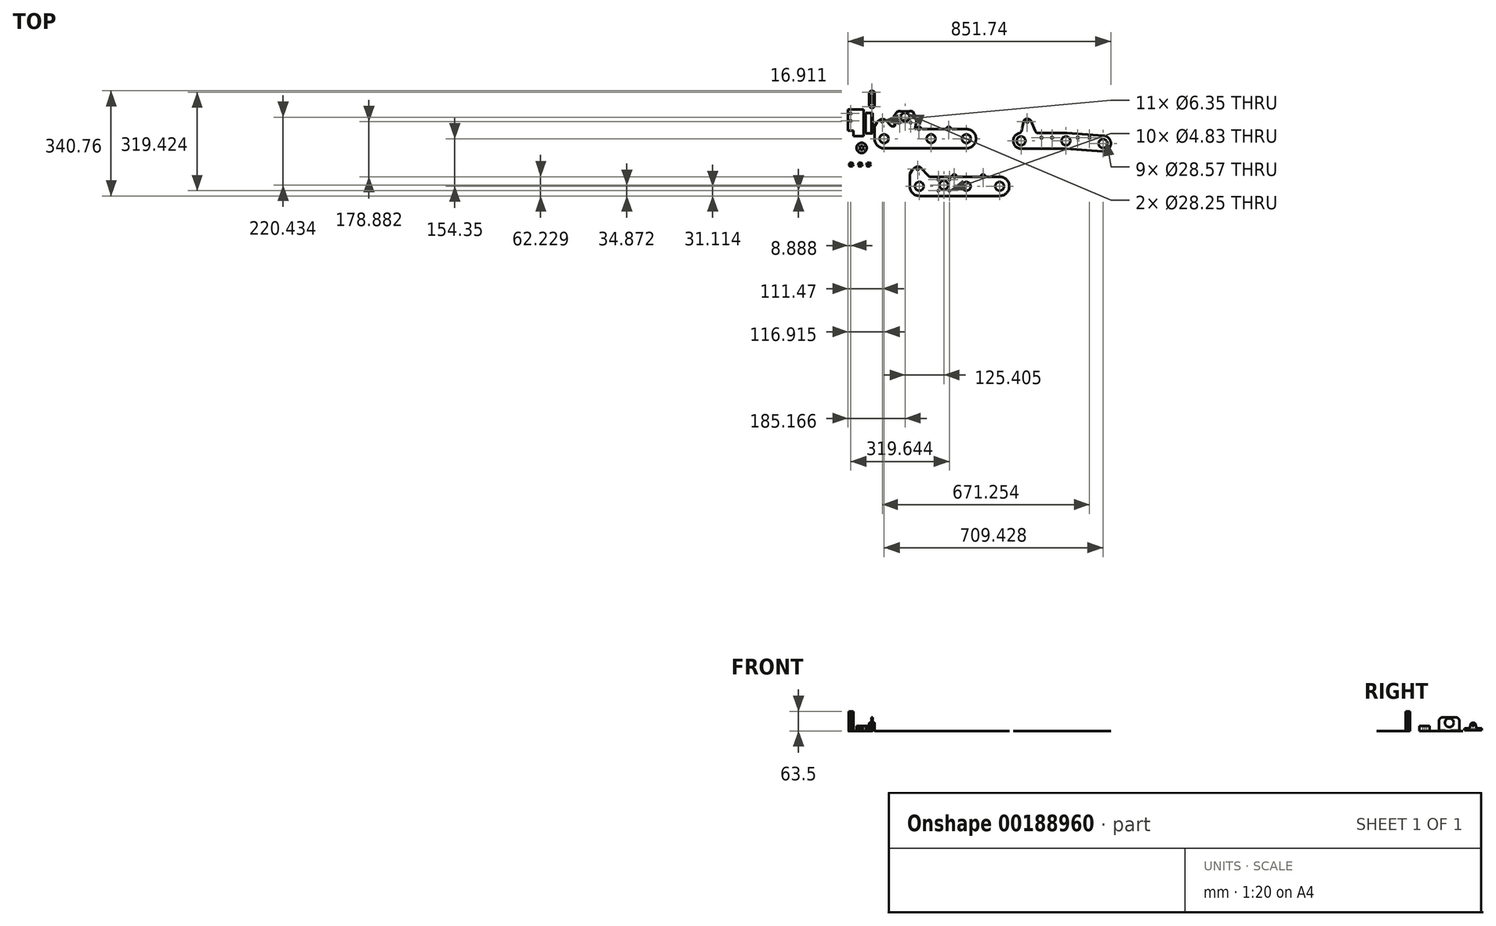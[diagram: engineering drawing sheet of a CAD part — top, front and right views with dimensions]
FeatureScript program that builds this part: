
annotation { "Feature Type Name" : "Feature", "Feature Type Description" : "" }
export const myFeature = defineFeature(function(context is Context, id is Id, definition is map)
    precondition{}
    {
        {
            assignVariable(context, id + "F0", {"name" : "width", "anyValue" : 16});
        }
        {
            var Q0;
            Q0=qCreatedBy(makeId("Top.planeOp"),FACE);
            var sketch = newSketch(context, id + "F1", { "sketchPlane" : qUnion([Q0])});
            skLineSegment(sketch, "E0", {"start": v(-68.88, 77.6) * mm, "end": v(-68.88, 9.01) * mm});
            skLineSegment(sketch, "E1", {"start": v(-68.88, 9.01) * mm, "end": v(-51.1, 9.01) * mm});
            skLineSegment(sketch, "E2", {"start": v(-51.1, 9.01) * mm, "end": v(-51.1, -8.77) * mm});
            skLineSegment(sketch, "E3", {"start": v(-51.1, -8.77) * mm, "end": v(-18.08, -8.77) * mm});
            skLineSegment(sketch, "E4", {"start": v(-18.08, -8.77) * mm, "end": v(-18.08, 9.01) * mm});
            skLineSegment(sketch, "E5", {"start": v(-18.08, 9.01) * mm, "end": v(-18.08, 77.6) * mm});
            skLineSegment(sketch, "E6", {"start": v(-18.08, 77.6) * mm, "end": v(-68.88, 77.6) * mm});
            skPoint(sketch, "E7", {"position": v(-60, 9.01) * mm});
            skCircle(sketch, "E8", {"center": v(-60, 40.12) * mm, "radius": 2.41 * mm});
            skCircle(sketch, "E9", {"center": v(-60, 64.05) * mm, "radius": 2.41 * mm});
            skLineSegment(sketch, "E10", {"start": v(-60, 40.12) * mm, "end": v(-60, 64.05) * mm, "construction": true});
            skSolve(sketch);
        }
        {
            var Q0;
            Q0=makeQuery(id+"F1.imprint","IMPRINT",FACE,{"disambiguationData":[TD([[makeQuery(id+"F1.imprint","IMPRINT",EDGE,{"derivedFrom":sQuery(id+"F1.wireOp",EDGE,"E0")}),1.0]])]});
            extrude(context, id + "F2", {"entities" : qUnion([Q0]), "depth" : 1 / 203.2 * mm});
        }
        {
            var Q0;
            Q0=qCreatedBy(makeId("Front.planeOp"),FACE);
            var sketch = newSketch(context, id + "F3", { "sketchPlane" : qUnion([Q0])});
            skLineSegment(sketch, "E11", {"start": v(-11.91, 0) * mm, "end": v(10.31, 0) * mm});
            skLineSegment(sketch, "E12", {"start": v(10.31, 0) * mm, "end": v(10.31, 44.45) * mm});
            skLineSegment(sketch, "E13", {"start": v(10.31, 44.45) * mm, "end": v(7.14, 44.45) * mm});
            skLineSegment(sketch, "E14", {"start": v(7.14, 44.45) * mm, "end": v(7.14, 3.18) * mm});
            skLineSegment(sketch, "E15", {"start": v(7.14, 3.18) * mm, "end": v(-11.91, 3.18) * mm});
            skLineSegment(sketch, "E16", {"start": v(-11.91, 3.17) * mm, "end": v(-11.91, 0) * mm});
            skSolve(sketch);
        }
        {
            var Q0;
            Q0 = qSketchRegion(id + "F3", true);
            extrude(context, id + "F4", {"entities" : qUnion([Q0]), "oppositeDirection" : true, "depth" : 66.04 * mm});
        }
        {
            var Q0;
            Q0=makeQuery(id+"F4.opExtrude","CAP_EDGE",EDGE,{"disambiguationData":[OSD([sQuery(id+"F3.wireOp",EDGE,"E13")])],"isStart":true});
            var Q1;
            Q1=makeQuery(id+"F4.opExtrude","CAP_EDGE",EDGE,{"disambiguationData":[OSD([sQuery(id+"F3.wireOp",EDGE,"E13")])],"isStart":false});
            chamfer(context, id + "F5", {"entities" : qUnion([Q0, Q1]), "width" : 7.62 * mm, "tangentPropagation" : true});
        }
        {
            var Q0;
            Q0=makeQuery(id+"F4.opExtrude","SWEPT_FACE",FACE,{"disambiguationData":[OSD([sQuery(id+"F3.wireOp",EDGE,"E12")])]});
            var sketch = newSketch(context, id + "F6", { "sketchPlane" : qUnion([Q0])});
            skCircle(sketch, "E17", {"center": v(33.02, 26.35) * mm, "radius": 14.29 * mm});
            skPoint(sketch, "E17.centerSnap0", {"position": v(33.02, 44.45) * mm});
            skSolve(sketch);
        }
        {
            var Q0;
            Q0 = qSketchRegion(id + "F6", true);
            extrude(context, id + "F7", {"entities" : qUnion([Q0]), "operationType" : NewBodyOperationType.REMOVE, "endBound" : BoundingType.THROUGH_ALL, "oppositeDirection" : true, "depth" : 25.4 * mm});
        }
        {
            var Q0;
            Q0=qCreatedBy(makeId("Top.planeOp"),FACE);
            var sketch = newSketch(context, id + "F8", { "sketchPlane" : qUnion([Q0])});
            skCircle(sketch, "E18", {"center": v(-29.26, -101.4) * mm, "radius": 2.55 * mm});
            skCircle(sketch, "E19.cCircle", {"center": v(-29.26, -101.4) * mm, "radius": 6.42 * mm, "construction": true});
            skLineSegment(sketch, "E19.0", {"start": v(-21.93, -100.32) * mm, "end": v(-24.66, -107.21) * mm});
            skLineSegment(sketch, "E19.1", {"start": v(-24.66, -107.21) * mm, "end": v(-32, -108.3) * mm});
            skLineSegment(sketch, "E19.2", {"start": v(-32, -108.3) * mm, "end": v(-36.6, -102.48) * mm});
            skLineSegment(sketch, "E19.3", {"start": v(-36.6, -102.48) * mm, "end": v(-33.86, -95.6) * mm});
            skLineSegment(sketch, "E19.4", {"start": v(-33.86, -95.6) * mm, "end": v(-26.53, -94.51) * mm});
            skLineSegment(sketch, "E19.5", {"start": v(-26.53, -94.51) * mm, "end": v(-21.93, -100.32) * mm});
            skPoint(sketch, "E19.0.midPoint", {"position": v(-23.3, -103.77) * mm});
            skCircle(sketch, "E20", {"center": v(-58.64, -101.4) * mm, "radius": 2.55 * mm});
            skCircle(sketch, "E21.cCircle", {"center": v(-58.64, -101.4) * mm, "radius": 6.42 * mm, "construction": true});
            skLineSegment(sketch, "E21.0", {"start": v(-51.3, -100.32) * mm, "end": v(-54.04, -107.21) * mm});
            skLineSegment(sketch, "E21.1", {"start": v(-54.04, -107.21) * mm, "end": v(-61.37, -108.3) * mm});
            skLineSegment(sketch, "E21.2", {"start": v(-61.37, -108.3) * mm, "end": v(-65.97, -102.48) * mm});
            skLineSegment(sketch, "E21.3", {"start": v(-65.97, -102.48) * mm, "end": v(-63.24, -95.6) * mm});
            skLineSegment(sketch, "E21.4", {"start": v(-63.24, -95.6) * mm, "end": v(-55.9, -94.51) * mm});
            skLineSegment(sketch, "E21.5", {"start": v(-55.9, -94.51) * mm, "end": v(-51.3, -100.32) * mm});
            skPoint(sketch, "E21.0.midPoint", {"position": v(-52.67, -103.77) * mm});
            skCircle(sketch, "E22", {"center": v(-2.45, -101.4) * mm, "radius": 2.55 * mm});
            skCircle(sketch, "E23.cCircle", {"center": v(-2.45, -101.4) * mm, "radius": 6.42 * mm, "construction": true});
            skLineSegment(sketch, "E23.0", {"start": v(4.88, -100.32) * mm, "end": v(2.15, -107.21) * mm});
            skLineSegment(sketch, "E23.1", {"start": v(2.15, -107.21) * mm, "end": v(-5.19, -108.3) * mm});
            skLineSegment(sketch, "E23.2", {"start": v(-5.19, -108.3) * mm, "end": v(-9.79, -102.48) * mm});
            skLineSegment(sketch, "E23.3", {"start": v(-9.79, -102.48) * mm, "end": v(-7.06, -95.6) * mm});
            skLineSegment(sketch, "E23.4", {"start": v(-7.06, -95.6) * mm, "end": v(0.28, -94.51) * mm});
            skLineSegment(sketch, "E23.5", {"start": v(0.28, -94.51) * mm, "end": v(4.88, -100.32) * mm});
            skPoint(sketch, "E23.0.midPoint", {"position": v(3.51, -103.77) * mm});
            skSolve(sketch);
        }
        {
            var Q0;
            Q0=makeQuery(id+"F8.imprint","IMPRINT",FACE,{"disambiguationData":[TD([[makeQuery(id+"F8.imprint","IMPRINT",EDGE,{"derivedFrom":sQuery(id+"F8.wireOp",EDGE,"E18")}),-1.0]])]});
            extrude(context, id + "F9", {"entities" : qUnion([Q0]), "depth" : (getVariable(context, 'width')) * mm});
        }
        {
            var Q0;
            Q0=makeQuery(id+"F8.imprint","IMPRINT",FACE,{"disambiguationData":[TD([[makeQuery(id+"F8.imprint","IMPRINT",EDGE,{"derivedFrom":sQuery(id+"F8.wireOp",EDGE,"E20")}),-1.0]])]});
            extrude(context, id + "F10", {"entities" : qUnion([Q0]), "depth" : 63.5 * mm});
        }
        {
            var Q0;
            Q0=makeQuery(id+"F8.imprint","IMPRINT",FACE,{"disambiguationData":[TD([[makeQuery(id+"F8.imprint","IMPRINT",EDGE,{"derivedFrom":sQuery(id+"F8.wireOp",EDGE,"E22")}),-1.0]])]});
            extrude(context, id + "F11", {"entities" : qUnion([Q0]), "depth" : (getVariable(context, 'width') - 0.25) * mm});
        }
        {
            var Q0;
            Q0=qCreatedBy(makeId("Top.planeOp"),FACE);
            var sketch = newSketch(context, id + "F12", { "sketchPlane" : qUnion([Q0])});
            skCircle(sketch, "E24", {"center": v(48.04, -17.33) * mm, "radius": 14.29 * mm});
            skCircle(sketch, "E25", {"center": v(48.04, -17.33) * mm, "radius": 31.12 * mm});
            skCircle(sketch, "E26", {"center": v(200.14, -17.33) * mm, "radius": 14.29 * mm});
            skCircle(sketch, "E27", {"center": v(200.14, -17.33) * mm, "radius": 31.12 * mm});
            skCircle(sketch, "E28", {"center": v(314.74, -17.33) * mm, "radius": 14.29 * mm});
            skCircle(sketch, "E29", {"center": v(314.74, -17.33) * mm, "radius": 31.12 * mm});
            skLineSegment(sketch, "E30", {"start": v(200.14, -17.33) * mm, "end": v(314.74, -17.33) * mm, "construction": true});
            skPoint(sketch, "E31", {"position": v(257.44, -17.33) * mm});
            skCircle(sketch, "E32", {"center": v(98.33, 70.48) * mm, "radius": 2.41 * mm});
            skCircle(sketch, "E33", {"center": v(134.25, 70.48) * mm, "radius": 2.41 * mm});
            skCircle(sketch, "E34", {"center": v(134.25, 34.55) * mm, "radius": 2.41 * mm});
            skCircle(sketch, "E35", {"center": v(98.33, 34.55) * mm, "radius": 2.41 * mm});
            skCircle(sketch, "E36", {"center": v(116.29, 52.52) * mm, "radius": 14.12 * mm});
            skLineSegment(sketch, "E37", {"start": v(37.93, 45.94) * mm, "end": v(49.3, 45.94) * mm});
            skLineSegment(sketch, "E38", {"start": v(16.92, 23) * mm, "end": v(16.92, -17.33) * mm});
            skPoint(sketch, "E39.start.orphan", {"position": v(48.04, 13.79) * mm});
            skLineSegment(sketch, "E40", {"start": v(49.3, 45.94) * mm, "end": v(76.65, 17.66) * mm});
            skCircle(sketch, "E41", {"center": v(42.6, 38.32) * mm, "radius": 3.18 * mm});
            skCircle(sketch, "E42", {"center": v(116.29, 52.52) * mm, "radius": 25.4 * mm, "construction": true});
            skCircle(sketch, "E43", {"center": v(257.44, 13.79) * mm, "radius": 3.18 * mm});
            skLineSegment(sketch, "E44", {"start": v(314.74, 13.79) * mm, "end": v(265.06, 13.79) * mm});
            skLineSegment(sketch, "E45", {"start": v(48.04, -48.44) * mm, "end": v(314.74, -48.44) * mm});
            skLineSegment(sketch, "E46", {"start": v(98.33, 70.48) * mm, "end": v(98.33, 34.55) * mm, "construction": true});
            skLineSegment(sketch, "E47", {"start": v(98.33, 70.48) * mm, "end": v(134.25, 70.48) * mm, "construction": true});
            skLineSegment(sketch, "E48", {"start": v(134.25, 34.55) * mm, "end": v(134.25, 70.48) * mm, "construction": true});
            skLineSegment(sketch, "E49", {"start": v(134.25, 34.55) * mm, "end": v(98.33, 34.55) * mm, "construction": true});
            skArc(sketch, "E50", {"start": v(265.06, 13.79) * mm, "mid": v(257.44, 21.4) * mm, "end": v(249.82, 13.79) * mm});
            skLineSegment(sketch, "E51.trimOffspring", {"start": v(249.82, 13.79) * mm, "end": v(168.77, 13.79) * mm});
            skCircle(sketch, "E52", {"center": v(161.15, 13.79) * mm, "radius": 3.18 * mm});
            skArc(sketch, "E53", {"start": v(168.77, 13.79) * mm, "mid": v(161.15, 21.4) * mm, "end": v(153.53, 13.79) * mm});
            skLineSegment(sketch, "E54.trimOffspring", {"start": v(153.53, 13.79) * mm, "end": v(147.77, 13.79) * mm});
            skLineSegment(sketch, "E55", {"start": v(25.83, 37.73) * mm, "end": v(37.93, 45.94) * mm});
            skLineSegment(sketch, "E56", {"start": v(16.92, 23) * mm, "end": v(25.83, 37.73) * mm});
            skCircle(sketch, "E57", {"center": v(162.29, -171.68) * mm, "radius": 14.29 * mm});
            skCircle(sketch, "E58", {"center": v(162.29, -171.68) * mm, "radius": 31.12 * mm});
            skCircle(sketch, "E59", {"center": v(314.4, -171.68) * mm, "radius": 14.29 * mm});
            skCircle(sketch, "E60", {"center": v(314.4, -171.68) * mm, "radius": 31.12 * mm});
            skCircle(sketch, "E61", {"center": v(422.6, -171.68) * mm, "radius": 14.29 * mm});
            skCircle(sketch, "E62", {"center": v(422.6, -171.68) * mm, "radius": 31.12 * mm});
            skLineSegment(sketch, "E63", {"start": v(314.4, -171.68) * mm, "end": v(422.6, -171.68) * mm, "construction": true});
            skPoint(sketch, "E64", {"position": v(368.5, -171.68) * mm});
            skCircle(sketch, "E65", {"center": v(223.73, -149.96) * mm, "radius": 2.41 * mm});
            skCircle(sketch, "E66", {"center": v(259.65, -149.96) * mm, "radius": 2.41 * mm});
            skCircle(sketch, "E67", {"center": v(259.65, -185.88) * mm, "radius": 2.41 * mm});
            skCircle(sketch, "E68", {"center": v(223.73, -185.88) * mm, "radius": 2.41 * mm});
            skCircle(sketch, "E69", {"center": v(241.7, -167.92) * mm, "radius": 14.12 * mm});
            skLineSegment(sketch, "E70", {"start": v(152.19, -108.41) * mm, "end": v(163.55, -108.41) * mm});
            skLineSegment(sketch, "E71", {"start": v(131.17, -131.36) * mm, "end": v(131.17, -171.68) * mm});
            skPoint(sketch, "E72.start.orphan", {"position": v(162.29, -140.56) * mm});
            skLineSegment(sketch, "E73", {"start": v(163.55, -108.41) * mm, "end": v(194.64, -140.56) * mm});
            skCircle(sketch, "E74", {"center": v(156.84, -116.03) * mm, "radius": 3.18 * mm});
            skCircle(sketch, "E75", {"center": v(241.7, -167.92) * mm, "radius": 25.4 * mm, "construction": true});
            skCircle(sketch, "E76", {"center": v(368.5, -140.56) * mm, "radius": 3.18 * mm});
            skLineSegment(sketch, "E77", {"start": v(422.6, -140.56) * mm, "end": v(376.12, -140.56) * mm});
            skLineSegment(sketch, "E78", {"start": v(162.29, -202.8) * mm, "end": v(422.6, -202.8) * mm});
            skLineSegment(sketch, "E79", {"start": v(223.73, -149.96) * mm, "end": v(223.73, -185.88) * mm, "construction": true});
            skLineSegment(sketch, "E80", {"start": v(223.73, -149.96) * mm, "end": v(259.65, -149.96) * mm, "construction": true});
            skLineSegment(sketch, "E81", {"start": v(259.65, -185.88) * mm, "end": v(259.65, -149.96) * mm, "construction": true});
            skLineSegment(sketch, "E82", {"start": v(259.65, -185.88) * mm, "end": v(223.73, -185.88) * mm, "construction": true});
            skArc(sketch, "E83", {"start": v(376.12, -140.56) * mm, "mid": v(368.5, -132.94) * mm, "end": v(360.88, -140.56) * mm});
            skLineSegment(sketch, "E84.trimOffspring", {"start": v(360.88, -140.56) * mm, "end": v(283.02, -140.56) * mm});
            skCircle(sketch, "E85", {"center": v(275.4, -140.56) * mm, "radius": 3.18 * mm});
            skArc(sketch, "E86", {"start": v(283.02, -140.56) * mm, "mid": v(275.4, -132.94) * mm, "end": v(267.78, -140.56) * mm});
            skLineSegment(sketch, "E87.trimOffspring", {"start": v(267.78, -140.56) * mm, "end": v(194.64, -140.56) * mm});
            skLineSegment(sketch, "E88", {"start": v(140.09, -116.62) * mm, "end": v(152.19, -108.41) * mm});
            skLineSegment(sketch, "E89", {"start": v(131.17, -131.36) * mm, "end": v(140.09, -116.62) * mm});
            skLineSegment(sketch, "E90", {"start": v(83.68, 25.08) * mm, "end": v(78.8, 53.19) * mm});
            skLineSegment(sketch, "E91", {"start": v(90.78, 70.97) * mm, "end": v(141.11, 70.97) * mm});
            skLineSegment(sketch, "E92", {"start": v(153.2, 39.74) * mm, "end": v(147.77, 13.79) * mm});
            skLineSegment(sketch, "E93", {"start": v(78.8, 53.19) * mm, "end": v(90.78, 70.97) * mm});
            skLineSegment(sketch, "E94", {"start": v(83.68, 25.08) * mm, "end": v(76.65, 17.66) * mm});
            skLineSegment(sketch, "E95", {"start": v(141.11, 70.97) * mm, "end": v(153.2, 39.74) * mm});
            skCircle(sketch, "E96", {"center": v(491.8, -24.42) * mm, "radius": 14.29 * mm});
            skArc(sketch, "E97", {"start": v(491.8, 0.98) * mm, "mid": v(466.4, -24.42) * mm, "end": v(491.8, -49.82) * mm});
            skCircle(sketch, "E98", {"center": v(511.93, 37.73) * mm, "radius": 3.18 * mm});
            skCircle(sketch, "E99", {"center": v(637.25, -24.42) * mm, "radius": 14.29 * mm});
            skArc(sketch, "E100", {"start": v(640.85, 0.72) * mm, "mid": v(639.05, 0.91) * mm, "end": v(637.25, 0.98) * mm});
            skArc(sketch, "E101", {"start": v(755.65, -58.31) * mm, "mid": v(782.85, -33.89) * mm, "end": v(757.46, -7.58) * mm});
            skCircle(sketch, "E102", {"center": v(757.46, -32.98) * mm, "radius": 14.29 * mm});
            skLineSegment(sketch, "E103", {"start": v(540.54, 0.98) * mm, "end": v(637.25, 0.98) * mm});
            skLineSegment(sketch, "E104", {"start": v(491.8, -49.82) * mm, "end": v(637.25, -49.82) * mm});
            skLineSegment(sketch, "E105", {"start": v(637.25, -49.82) * mm, "end": v(757.46, -58.45) * mm});
            skLineSegment(sketch, "E106", {"start": v(637.25, 0.98) * mm, "end": v(757.46, -7.58) * mm});
            skLineSegment(sketch, "E107", {"start": v(491.8, 0.98) * mm, "end": v(501.87, 46.58) * mm});
            skLineSegment(sketch, "E108", {"start": v(501.87, 46.58) * mm, "end": v(521.23, 46.58) * mm});
            skLineSegment(sketch, "E109", {"start": v(521.23, 46.58) * mm, "end": v(540.54, 0.98) * mm});
            skCircle(sketch, "E110", {"center": v(675.7, -14.15) * mm, "radius": 3.18 * mm});
            skCircle(sketch, "E111", {"center": v(713.84, -14.15) * mm, "radius": 3.18 * mm});
            skCircle(sketch, "E112", {"center": v(592.17, -14.15) * mm, "radius": 3.18 * mm});
            skCircle(sketch, "E113", {"center": v(558.28, -14.15) * mm, "radius": 3.18 * mm});
            skSolve(sketch);
        }
        {
            var Q0;
            Q0 = qSketchRegion(id + "F12", true);
            extrude(context, id + "F13", {"entities" : qUnion([Q0]), "depth" : 1 / 203.2 * mm});
        }
        {
            var Q0;
            Q0=makeQuery(id+"F13.opExtrude","SWEPT_EDGE",EDGE,{"disambiguationData":[OSD([sQuery(id+"F12.wireOp",EDGE,"zGA84i3n-rNFC-Hxu3-0g7T-5ZzaSlM4ImFY"),sQuery(id+"F12.wireOp",EDGE,"E40")])]});
            var Q1;
            Q1=makeQuery(id+"F13.opExtrude","SWEPT_EDGE",EDGE,{"disambiguationData":[OSD([sQuery(id+"F12.wireOp",EDGE,"E37"),sQuery(id+"F12.wireOp",EDGE,"E40")])]});
            var Q2;
            Q2=makeQuery(id+"F13.opExtrude","SWEPT_EDGE",EDGE,{"disambiguationData":[OSD([sQuery(id+"F12.wireOp",EDGE,"E37"),sQuery(id+"F12.wireOp",EDGE,"E38")])]});
            var Q3;
            Q3=makeQuery(id+"F13.opExtrude","SWEPT_EDGE",EDGE,{"disambiguationData":[OSD([sQuery(id+"F12.wireOp",EDGE,"SkITifCB-E90i-DBId-o6hG-ZY5qo694HUbQ"),sQuery(id+"F12.wireOp",EDGE,"nln1uN2U-nkBP-hW6Q-JO62-WThQ14yejk3Z")])]});
            var Q4;
            Q4=makeQuery(id+"F13.opExtrude","SWEPT_EDGE",EDGE,{"disambiguationData":[OSD([sQuery(id+"F12.wireOp",EDGE,"E29"),sQuery(id+"F12.wireOp",EDGE,"L0iEf99Y-L2M9-QqnG-EvBq-umjeq94Xu7fE"),sQuery(id+"F12.wireOp",EDGE,"SkITifCB-E90i-DBId-o6hG-ZY5qo694HUbQ")])]});
            var Q5;
            Q5=makeQuery(id+"F13.opExtrude","SWEPT_EDGE",EDGE,{"disambiguationData":[OSD([sQuery(id+"F12.wireOp",EDGE,"nln1uN2U-nkBP-hW6Q-JO62-WThQ14yejk3Z"),sQuery(id+"F12.wireOp",EDGE,"l49saghn-IAAb-vpga-oE1Y-PDr44z0bv9VA")])]});
            var Q6;
            Q6=makeQuery(id+"F13.opExtrude","SWEPT_EDGE",EDGE,{"disambiguationData":[OSD([sQuery(id+"F12.wireOp",EDGE,"E50"),sQuery(id+"F12.wireOp",EDGE,"E51.trimOffspring")])]});
            var Q7;
            Q7=makeQuery(id+"F13.opExtrude","SWEPT_EDGE",EDGE,{"disambiguationData":[OSD([sQuery(id+"F12.wireOp",EDGE,"E44"),sQuery(id+"F12.wireOp",EDGE,"E50")])]});
            var Q8;
            Q8=makeQuery(id+"F13.opExtrude","SWEPT_EDGE",EDGE,{"disambiguationData":[OSD([sQuery(id+"F12.wireOp",EDGE,"E51.trimOffspring"),sQuery(id+"F12.wireOp",EDGE,"E53")])]});
            var Q9;
            Q9=makeQuery(id+"F13.opExtrude","SWEPT_EDGE",EDGE,{"disambiguationData":[OSD([sQuery(id+"F12.wireOp",EDGE,"E53"),sQuery(id+"F12.wireOp",EDGE,"E54.trimOffspring")])]});
            var Q10;
            Q10=makeQuery(id+"F13.opExtrude","SWEPT_EDGE",EDGE,{"disambiguationData":[OSD([sQuery(id+"F12.wireOp",EDGE,"E55"),sQuery(id+"F12.wireOp",EDGE,"E56")])]});
            var Q11;
            Q11=makeQuery(id+"F13.opExtrude","SWEPT_EDGE",EDGE,{"disambiguationData":[OSD([sQuery(id+"F12.wireOp",EDGE,"E107"),sQuery(id+"F12.wireOp",EDGE,"E108")])]});
            var Q12;
            Q12=makeQuery(id+"F13.opExtrude","SWEPT_EDGE",EDGE,{"disambiguationData":[OSD([sQuery(id+"F12.wireOp",EDGE,"E108"),sQuery(id+"F12.wireOp",EDGE,"E109")])]});
            var Q13;
            Q13=makeQuery(id+"F13.opExtrude","SWEPT_EDGE",EDGE,{"disambiguationData":[OSD([sQuery(id+"F12.wireOp",EDGE,"E103"),sQuery(id+"F12.wireOp",EDGE,"E109")])]});
            var Q14;
            Q14=makeQuery(id+"F13.opExtrude","SWEPT_EDGE",EDGE,{"disambiguationData":[OSD([sQuery(id+"F12.wireOp",EDGE,"E97"),sQuery(id+"F12.wireOp",EDGE,"E107")])]});
            var Q15;
            Q15=makeQuery(id+"F13.opExtrude","SWEPT_EDGE",EDGE,{"disambiguationData":[OSD([sQuery(id+"F12.wireOp",EDGE,"E100"),sQuery(id+"F12.wireOp",EDGE,"E106")])]});
            var Q16;
            Q16=makeQuery(id+"F13.opExtrude","SWEPT_EDGE",EDGE,{"disambiguationData":[OSD([sQuery(id+"F12.wireOp",EDGE,"E100"),sQuery(id+"F12.wireOp",EDGE,"E103"),sQuery(id+"F12.wireOp",EDGE,"E106")])]});
            fillet(context, id + "F14", {"entities" : qUnion([Q0, Q1, Q2, Q3, Q4, Q5, Q6, Q7, Q8, Q9, Q10, Q11, Q12, Q13, Q14, Q15, Q16]), "radius" : 10.16 * mm, "tangentPropagation" : true, "allowEdgeOverflow" : false});
        }
        {
            var Q0;
            Q0=qCreatedBy(makeId("Right.planeOp"),FACE);
            var sketch = newSketch(context, id + "F15", { "sketchPlane" : qUnion([Q0])});
            skLineSegment(sketch, "E114.bottom", {"start": v(129.08, 7.8) * mm, "end": v(121.36, 7.8) * mm});
            skLineSegment(sketch, "E114.top", {"start": v(129.08, 1.44) * mm, "end": v(90.98, 1.44) * mm});
            skLineSegment(sketch, "E114.left", {"start": v(129.08, 7.8) * mm, "end": v(129.08, 1.44) * mm});
            skLineSegment(sketch, "E114.right", {"start": v(90.98, 7.8) * mm, "end": v(90.98, 1.44) * mm});
            skLineSegment(sketch, "E115.trimOffspring", {"start": v(98.7, 7.8) * mm, "end": v(90.98, 7.8) * mm});
            skPoint(sketch, "E116", {"position": v(110.03, 1.44) * mm});
            skCircle(sketch, "E117", {"center": v(110.03, 18.83) * mm, "radius": 3.18 * mm});
            skLineSegment(sketch, "E118", {"start": v(121.36, 7.8) * mm, "end": v(117.6, 21.99) * mm});
            skLineSegment(sketch, "E119", {"start": v(112.69, 25.77) * mm, "end": v(107.37, 25.77) * mm});
            skLineSegment(sketch, "E120", {"start": v(102.46, 21.99) * mm, "end": v(98.7, 7.8) * mm});
            skPoint(sketch, "E121.visualSharp", {"position": v(116.6, 25.77) * mm});
            skArc(sketch, "E121.filletArc", {"start": v(117.6, 21.99) * mm, "mid": v(115.79, 24.71) * mm, "end": v(112.69, 25.77) * mm});
            skPoint(sketch, "E122.visualSharp", {"position": v(103.46, 25.77) * mm});
            skArc(sketch, "E122.filletArc", {"start": v(107.37, 25.77) * mm, "mid": v(104.27, 24.71) * mm, "end": v(102.46, 21.99) * mm});
            skSolve(sketch);
        }
        {
            var Q0;
            Q0 = qSketchRegion(id + "F15", true);
            extrude(context, id + "F16", {"entities" : qUnion([Q0]), "depth" : 17.78 * mm});
        }
        {
            var Q0;
            Q0=makeQuery(id+"F16.opExtrude","SWEPT_FACE",FACE,{"disambiguationData":[OSD([sQuery(id+"F15.wireOp",EDGE,"E119")])]});
            var sketch = newSketch(context, id + "F17", { "sketchPlane" : qUnion([Q0])});
            skPoint(sketch, "E123", {"position": v(8.9, 110.03) * mm});
            skPoint(sketch, "E123.positionSnap0", {"position": v(0, 110.03) * mm});
            skPoint(sketch, "E123.positionSnap1", {"position": v(8.9, 112.69) * mm});
            skLineSegment(sketch, "E124.bottom", {"start": v(13.9, 88.44) * mm, "end": v(3.87, 88.44) * mm});
            skLineSegment(sketch, "E124.top", {"start": v(13.9, 131.62) * mm, "end": v(3.87, 131.62) * mm});
            skLineSegment(sketch, "E124.left", {"start": v(13.9, 88.44) * mm, "end": v(13.9, 131.62) * mm});
            skLineSegment(sketch, "E124.right", {"start": v(3.87, 88.44) * mm, "end": v(3.87, 131.62) * mm});
            skSolve(sketch);
        }
        {
            var Q0;
            Q0 = qSketchRegion(id + "F17", true);
            var Q1;
            Q1=makeQuery(id+"F16.opExtrude","SWEPT_FACE",FACE,{"disambiguationData":[OSD([sQuery(id+"F15.wireOp",EDGE,"E115.trimOffspring")])]});
            extrude(context, id + "F18", {"entities" : qUnion([Q0]), "operationType" : NewBodyOperationType.REMOVE, "endBound" : BoundingType.UP_TO_SURFACE, "oppositeDirection" : true, "endBoundEntityFace" : qUnion([Q1]), "depth" : 18.03 * mm});
        }
        {
            var Q0;
            {var subQ0=sQuery(id+"F15.wireOp",EDGE,"E120");var subQ1=sQuery(id+"F15.wireOp",EDGE,"E115.trimOffspring");Q0=makeQuery(id+"F18.boolean.opBoolean","SPLIT",EDGE,{"disambiguationData":[TD([makeQuery(id+"F18.opExtrude","SWEPT_FACE",FACE,{"disambiguationData":[OSD([sQuery(id+"F17.wireOp",EDGE,"E124.right")])]})])],"derivedFrom":makeQuery(id+"F16.opExtrude","SWEPT_EDGE",EDGE,{"disambiguationData":[OSD([subQ1,subQ0])]})});}
            var Q1;
            {var subQ0=sQuery(id+"F15.wireOp",EDGE,"E120");var subQ1=sQuery(id+"F15.wireOp",EDGE,"E115.trimOffspring");Q1=makeQuery(id+"F18.boolean.opBoolean","SPLIT",EDGE,{"disambiguationData":[TD([makeQuery(id+"F18.opExtrude","SWEPT_FACE",FACE,{"disambiguationData":[OSD([sQuery(id+"F17.wireOp",EDGE,"E124.left")])]})])],"derivedFrom":makeQuery(id+"F16.opExtrude","SWEPT_EDGE",EDGE,{"disambiguationData":[OSD([subQ1,subQ0])]})});}
            var Q2;
            {var subQ1=sQuery(id+"F15.wireOp",EDGE,"E118");var subQ2=sQuery(id+"F15.wireOp",EDGE,"E114.bottom");Q2=makeQuery(id+"F18.boolean.opBoolean","SPLIT",EDGE,{"disambiguationData":[TD([makeQuery(id+"F18.opExtrude","SWEPT_FACE",FACE,{"disambiguationData":[OSD([sQuery(id+"F17.wireOp",EDGE,"E124.right")])]})])],"derivedFrom":makeQuery(id+"F16.opExtrude","SWEPT_EDGE",EDGE,{"disambiguationData":[OSD([subQ2,subQ1])]})});}
            var Q3;
            {var subQ1=sQuery(id+"F15.wireOp",EDGE,"E118");var subQ2=sQuery(id+"F15.wireOp",EDGE,"E114.bottom");Q3=makeQuery(id+"F18.boolean.opBoolean","SPLIT",EDGE,{"disambiguationData":[TD([makeQuery(id+"F18.opExtrude","SWEPT_FACE",FACE,{"disambiguationData":[OSD([sQuery(id+"F17.wireOp",EDGE,"E124.left")])]})])],"derivedFrom":makeQuery(id+"F16.opExtrude","SWEPT_EDGE",EDGE,{"disambiguationData":[OSD([subQ2,subQ1])]})});}
            fillet(context, id + "F19", {"entities" : qUnion([Q0, Q1, Q2, Q3]), "radius" : 5.08 * mm, "tangentPropagation" : true, "allowEdgeOverflow" : false});
        }
        {
            var Q0;
            Q0=makeQuery(id+"F16.opExtrude","SWEPT_FACE",FACE,{"disambiguationData":[OSD([sQuery(id+"F15.wireOp",EDGE,"E114.top")])]});
            var sketch = newSketch(context, id + "F20", { "sketchPlane" : qUnion([Q0])});
            skArc(sketch, "E125", {"start": v(17.78, -90.98) * mm, "mid": v(8.9, -82.09) * mm, "end": v(0, -90.98) * mm});
            skArc(sketch, "E126", {"start": v(0, -129.08) * mm, "mid": v(8.9, -137.97) * mm, "end": v(17.78, -129.08) * mm});
            skLineSegment(sketch, "E127.0", {"start": v(17.78, -90.98) * mm, "end": v(0, -90.98) * mm});
            skPoint(sketch, "E128.0", {"position": v(0, -94.78) * mm});
            skPoint(sketch, "E129.0", {"position": v(17.78, -107.37) * mm});
            skLineSegment(sketch, "E130.0", {"start": v(17.78, -129.08) * mm, "end": v(17.78, -90.98) * mm});
            skLineSegment(sketch, "E131.0", {"start": v(0, -129.08) * mm, "end": v(0, -90.98) * mm});
            skLineSegment(sketch, "E132.0", {"start": v(17.78, -129.08) * mm, "end": v(0, -129.08) * mm});
            skCircle(sketch, "E133", {"center": v(8.9, -86.5) * mm, "radius": 2.41 * mm});
            skCircle(sketch, "E134", {"center": v(8.9, -133.55) * mm, "radius": 2.41 * mm});
            skLineSegment(sketch, "E135", {"start": v(8.9, -86.5) * mm, "end": v(8.9, -90.98) * mm, "construction": true});
            skLineSegment(sketch, "E136", {"start": v(8.9, -129.08) * mm, "end": v(8.9, -133.55) * mm, "construction": true});
            skSolve(sketch);
        }
        {
            var Q0;
            Q0 = qSketchRegion(id + "F20", true);
            var Q1;
            {var subQ0=sQuery(id+"F15.wireOp",EDGE,"E115.trimOffspring");Q1=makeQuery(id+"F18.boolean.opBoolean","MERGE",FACE,{"derivedFrom":[makeQuery(id+"F16.opExtrude","SWEPT_FACE",FACE,{"disambiguationData":[OSD([sQuery(id+"F15.wireOp",EDGE,"E114.bottom")])]}),makeQuery(id+"F16.opExtrude","SWEPT_FACE",FACE,{"disambiguationData":[OSD([subQ0])]}),makeQuery(id+"F18.opExtrude","CAP_FACE",FACE,{"disambiguationData":[OSD([subQ0])],"isStart":false})]});}
            extrude(context, id + "F21", {"entities" : qUnion([Q0]), "operationType" : NewBodyOperationType.ADD, "endBound" : BoundingType.UP_TO_SURFACE, "oppositeDirection" : true, "endBoundEntityFace" : qUnion([Q1]), "depth" : 25.4 * mm});
        }
        {
            var Q0;
            Q0=qCreatedBy(makeId("Top.planeOp"),FACE);
            var sketch = newSketch(context, id + "F22", { "sketchPlane" : qUnion([Q0])});
            skCircle(sketch, "E137", {"center": v(-24.76, -47.34) * mm, "radius": 16.51 * mm});
            skCircle(sketch, "E138.cCircle", {"center": v(-24.76, -47.34) * mm, "radius": 6.54 * mm, "construction": true});
            skLineSegment(sketch, "E138.0", {"start": v(-20.98, -53.88) * mm, "end": v(-28.54, -53.88) * mm});
            skLineSegment(sketch, "E138.1", {"start": v(-28.54, -53.88) * mm, "end": v(-32.31, -47.34) * mm});
            skLineSegment(sketch, "E138.2", {"start": v(-32.31, -47.34) * mm, "end": v(-28.54, -40.8) * mm});
            skLineSegment(sketch, "E138.3", {"start": v(-28.54, -40.8) * mm, "end": v(-20.98, -40.8) * mm});
            skLineSegment(sketch, "E138.4", {"start": v(-20.98, -40.8) * mm, "end": v(-17.2, -47.34) * mm});
            skLineSegment(sketch, "E138.5", {"start": v(-17.2, -47.34) * mm, "end": v(-20.98, -53.88) * mm});
            skPoint(sketch, "E138.0.midPoint", {"position": v(-24.76, -53.88) * mm});
            skSolve(sketch);
        }
        {
            var Q0;
            Q0 = qSketchRegion(id + "F22", true);
            extrude(context, id + "F23", {"entities" : qUnion([Q0]), "depth" : 16.5 * mm});
        }
    });
